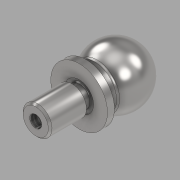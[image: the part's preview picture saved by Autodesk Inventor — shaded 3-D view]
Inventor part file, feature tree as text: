
AUTODESK INVENTOR PART (.ipt)
format: ipt  version: 2020 (Build 240168000, 168)  size: 173,568 bytes
history: native  units: in
note: dims shown in document units (in); Inventor stores cm internally (conversion verified against a paired STEP export)
features: fillet x2, sketch x2, other x1, revolve x1, chamfer x1, hole x1
ambient origin geometry x8: Origin, YZ Plane, XZ Plane, XY Plane, X Axis, Y Axis, Z Axis, Center Point
bodies: Body1 (feature_tree)
feature tree (8):
  other  "Sólido1"
  revolve  "Revolución1"  [1 undecoded]
  fillet  "Empalme_016"  Radius=0.375in
  fillet  "Empalme_031"  Radius=0.5in
  chamfer  "Chaflán1"  Distance=0.375in
  hole  "Agujero1"  [1 undecoded]
  sketch  "Boceto1"  dims[d0=0.25in d1=0.49in d2=0.375in d3=0.5in]
  sketch  "Boceto2"  dims[d4=0.313in d5=0.375in d7=0.688in d8=0.435in d9=0.016in d10=0.032in d11=0.375in d12=90.0deg d13=0.016in d15=0.031in d16=0.016in d17=0.125in d18=45.0deg d19=0.104in d20=0.181in d21=0.5in d22=0.3in d23=0.5635in d24=0.313in d25=0.8108in]
note: 2 required parameter values undecoded (feature->parameter linkage not recoverable at this tier; creation-order binding heuristic only, values carry confidence <= 0.55)